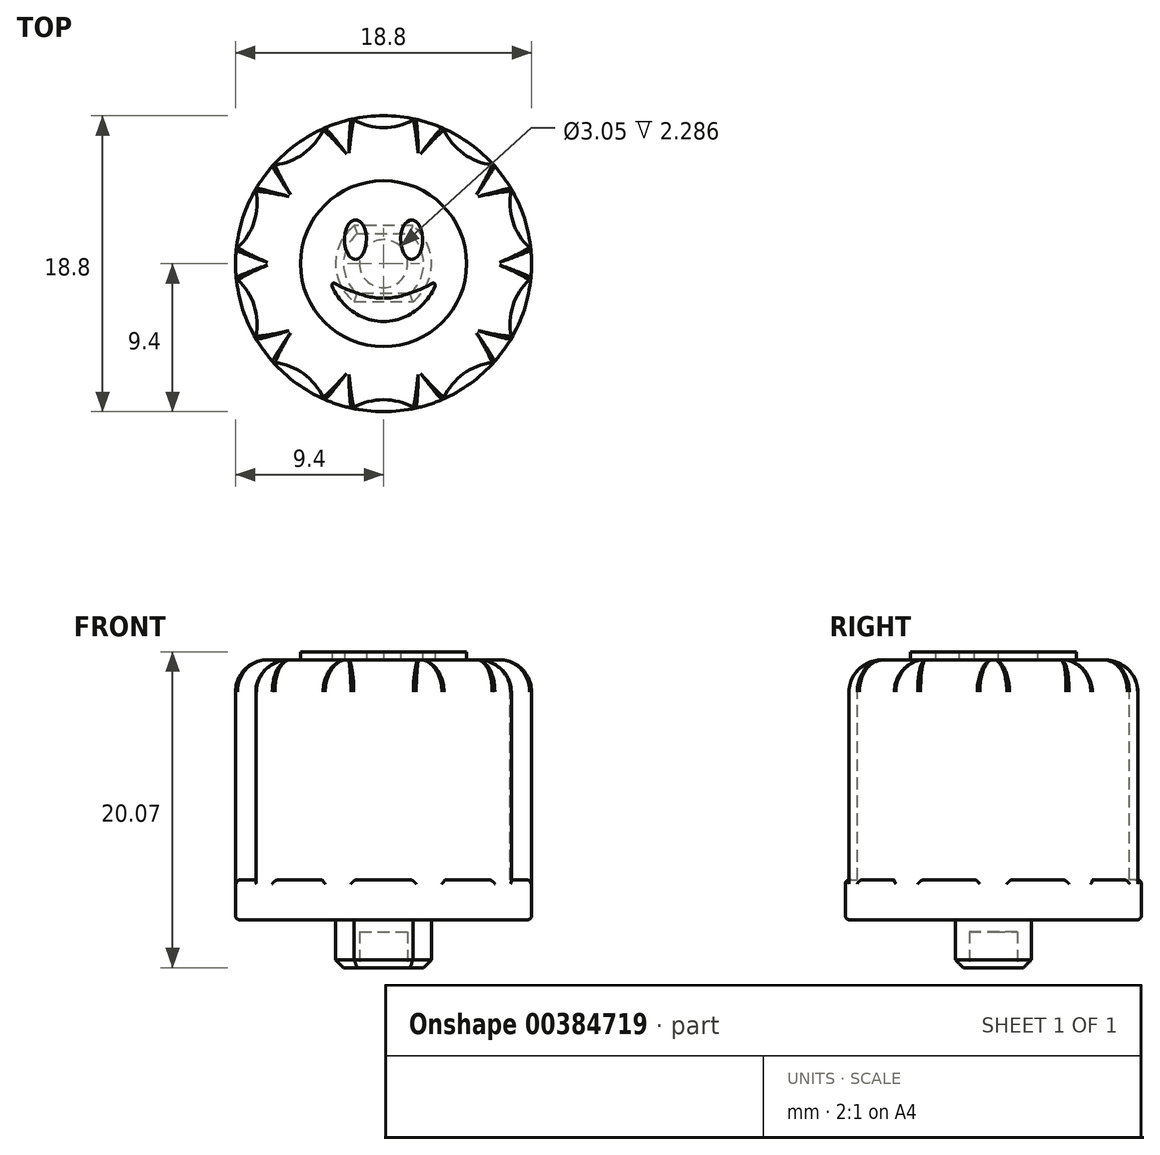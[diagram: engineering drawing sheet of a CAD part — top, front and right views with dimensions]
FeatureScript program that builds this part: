
annotation { "Feature Type Name" : "Feature", "Feature Type Description" : "" }
export const myFeature = defineFeature(function(context is Context, id is Id, definition is map)
    precondition{}
    {
        {
            var Q0;
            Q0=qCreatedBy(makeId("Top.planeOp"),FACE);
            var sketch = newSketch(context, id + "F0", { "sketchPlane" : qUnion([Q0])});
            skCircle(sketch, "E0", {"center": v(0, 0) * mm, "radius": 9.4 * mm});
            skSolve(sketch);
        }
        {
            var Q0;
            Q0=qSketchRegion(id+"F0",true);
            extrude(context, id + "F1", {"entities" : qUnion([Q0]), "depth" : 16.5 * mm});
        }
        {
            var Q0;
            Q0=makeQuery(id+"F1.opExtrude","CAP_FACE",FACE,{"disambiguationData":[OSD([sQuery(id+"F0.wireOp",EDGE,"E0")])],"isStart":false});
            var sketch = newSketch(context, id + "F2", { "sketchPlane" : qUnion([Q0])});
            skCircle(sketch, "E1.1.0", {"center": v(-7.32, 10.07) * mm, "radius": 3.81 * mm});
            skCircle(sketch, "E1.2.0", {"center": v(-11.84, 3.85) * mm, "radius": 3.81 * mm});
            skCircle(sketch, "E1.3.0", {"center": v(-11.84, -3.85) * mm, "radius": 3.81 * mm});
            skCircle(sketch, "E1.4.0", {"center": v(-7.32, -10.07) * mm, "radius": 3.81 * mm});
            skCircle(sketch, "E1.5.0", {"center": v(0, -12.45) * mm, "radius": 3.81 * mm});
            skCircle(sketch, "E1.6.0", {"center": v(7.32, -10.07) * mm, "radius": 3.81 * mm});
            skCircle(sketch, "E1.7.0", {"center": v(11.84, -3.85) * mm, "radius": 3.81 * mm});
            skCircle(sketch, "E1.8.0", {"center": v(11.84, 3.85) * mm, "radius": 3.81 * mm});
            skCircle(sketch, "E1.9.0", {"center": v(7.32, 10.07) * mm, "radius": 3.81 * mm});
            skPoint(sketch, "E1.center", {"position": v(0, 0) * mm});
            skPoint(sketch, "E2.center.orphan", {"position": v(0, 12.45) * mm});
            skCircle(sketch, "E3", {"center": v(0, 12.45) * mm, "radius": 3.81 * mm});
            skSolve(sketch);
        }
        {
            var Q0;
            Q0=qSketchRegion(id+"F2",true);
            extrude(context, id + "F3", {"entities" : qUnion([Q0]), "operationType" : NewBodyOperationType.REMOVE, "oppositeDirection" : true, "depth" : 13.97 * mm});
        }
        {
            var Q0;
            Q0=makeQuery(id+"F1.opExtrude","CAP_FACE",FACE,{"disambiguationData":[OSD([sQuery(id+"F0.wireOp",EDGE,"E0")])],"isStart":false});
            fillet(context, id + "F4", {"entities" : qUnion([Q0]), "radius" : 2.03 * mm, "tangentPropagation" : true, "allowEdgeOverflow" : false});
        }
        {
            var Q0;
            Q0=makeQuery(id+"F1.opExtrude","CAP_FACE",FACE,{"disambiguationData":[OSD([sQuery(id+"F0.wireOp",EDGE,"E0")])],"isStart":true});
            var sketch = newSketch(context, id + "F5", { "sketchPlane" : qUnion([Q0])});
            skCircle(sketch, "E4", {"center": v(0, 0) * mm, "radius": 5.33 * mm});
            skSolve(sketch);
        }
        {
            var Q0;
            Q0=qSketchRegion(id+"F5",true);
            extrude(context, id + "F6", {"entities" : qUnion([Q0]), "operationType" : NewBodyOperationType.ADD, "depth" : 8.25 * mm, "offsetDistance" : 25.4 * mm});
        }
        {
            var Q0;
            Q0=makeQuery(id+"F6.opExtrude","CAP_FACE",FACE,{"disambiguationData":[OSD([sQuery(id+"F5.wireOp",EDGE,"E4")])],"isStart":false});
            var sketch = newSketch(context, id + "F7", { "sketchPlane" : qUnion([Q0])});
            skCircle(sketch, "E5", {"center": v(0, 10.16) * mm, "radius": 5.72 * mm});
            skCircle(sketch, "E6.1.0", {"center": v(-9.66, 3.14) * mm, "radius": 5.72 * mm});
            skCircle(sketch, "E6.2.0", {"center": v(-5.97, -8.22) * mm, "radius": 5.72 * mm});
            skCircle(sketch, "E6.3.0", {"center": v(5.97, -8.22) * mm, "radius": 5.72 * mm});
            skCircle(sketch, "E6.4.0", {"center": v(9.66, 3.14) * mm, "radius": 5.72 * mm});
            skPoint(sketch, "E6.center", {"position": v(0, 0) * mm});
            skSolve(sketch);
        }
        {
            var Q0;
            Q0=qSketchRegion(id+"F7",true);
            extrude(context, id + "F8", {"entities" : qUnion([Q0]), "operationType" : NewBodyOperationType.REMOVE, "oppositeDirection" : true, "depth" : 7.62 * mm});
        }
        {
            var Q0;
            Q0=makeQuery(id+"F8.boolean.opBoolean","MERGE",FACE,{"derivedFrom":[makeQuery(id+"F1.opExtrude","CAP_FACE",FACE,{"disambiguationData":[OSD([sQuery(id+"F0.wireOp",EDGE,"E0")])],"isStart":true}),makeQuery(id+"F8.opExtrude","CAP_FACE",FACE,{"disambiguationData":[OSD([sQuery(id+"F7.wireOp",EDGE,"E5")])],"isStart":false}),makeQuery(id+"F8.opExtrude","CAP_FACE",FACE,{"disambiguationData":[OSD([sQuery(id+"F7.wireOp",EDGE,"E6.1.0")])],"isStart":false}),makeQuery(id+"F8.opExtrude","CAP_FACE",FACE,{"disambiguationData":[OSD([sQuery(id+"F7.wireOp",EDGE,"E6.2.0")])],"isStart":false}),makeQuery(id+"F8.opExtrude","CAP_FACE",FACE,{"disambiguationData":[OSD([sQuery(id+"F7.wireOp",EDGE,"E6.3.0")])],"isStart":false}),makeQuery(id+"F8.opExtrude","CAP_FACE",FACE,{"disambiguationData":[OSD([sQuery(id+"F7.wireOp",EDGE,"E6.4.0")])],"isStart":false})]});
            var sketch = newSketch(context, id + "F9", { "sketchPlane" : qUnion([Q0])});
            skCircle(sketch, "E7", {"center": v(0, 0) * mm, "radius": 6.22 * mm});
            skCircle(sketch, "E8", {"center": v(0, 0) * mm, "radius": 4.32 * mm});
            skSolve(sketch);
        }
        {
            var Q0;
            Q0=qSketchRegion(id+"F9",true);
            extrude(context, id + "F10", {"entities" : qUnion([Q0]), "operationType" : NewBodyOperationType.REMOVE, "depth" : 4.06 * mm, "offsetDistance" : 25.4 * mm});
        }
        {
            var Q0;
            Q0=makeQuery(id+"F10.boolean.opBoolean","MERGE",FACE,{"derivedFrom":[makeQuery(id+"F1.opExtrude","CAP_FACE",FACE,{"disambiguationData":[OSD([sQuery(id+"F0.wireOp",EDGE,"E0")])],"isStart":true}),makeQuery(id+"F10.opExtrude","CAP_FACE",FACE,{"disambiguationData":[OSD([sQuery(id+"F9.wireOp",EDGE,"E7"),sQuery(id+"F9.wireOp",EDGE,"E8")])],"isStart":true})]});
            var sketch = newSketch(context, id + "F11", { "sketchPlane" : qUnion([Q0])});
            skCircle(sketch, "E9", {"center": v(0, 0) * mm, "radius": 6.35 * mm});
            skSolve(sketch);
        }
        {
            var Q0;
            Q0=qSketchRegion(id+"F11",true);
            extrude(context, id + "F12", {"entities" : qUnion([Q0]), "operationType" : NewBodyOperationType.ADD, "depth" : 2.54 * mm, "offsetDistance" : 25.4 * mm});
        }
        {
            var Q0;
            Q0=makeQuery(id+"F6.opExtrude","CAP_FACE",FACE,{"disambiguationData":[OSD([sQuery(id+"F5.wireOp",EDGE,"E4")])],"isStart":false});
            fillet(context, id + "F13", {"entities" : qUnion([Q0]), "radius" : 0.5 * mm, "tangentPropagation" : true, "allowEdgeOverflow" : false});
        }
        {
            var Q0;
            Q0=makeQuery(id+"F12.opExtrude","CAP_EDGE",EDGE,{"disambiguationData":[OSD([sQuery(id+"F11.wireOp",EDGE,"E9")])],"isStart":false});
            var Q1;
            Q1=makeQuery(id+"F1.opExtrude","CAP_EDGE",EDGE,{"disambiguationData":[OSD([sQuery(id+"F0.wireOp",EDGE,"E0")])],"isStart":true});
            var Q2;
            Q2=makeQuery(id+"F3.boolean.opBoolean","INTERSECT",EDGE,{"derivedFrom":[makeQuery(id+"F1.opExtrude","SWEPT_FACE",FACE,{"disambiguationData":[OSD([sQuery(id+"F0.wireOp",EDGE,"E0")])]}),makeQuery(id+"F3.opExtrude","CAP_FACE",FACE,{"disambiguationData":[OSD([sQuery(id+"F2.wireOp",EDGE,"E1.4.0")])],"isStart":false})]});
            var Q3;
            Q3=makeQuery(id+"F3.boolean.opBoolean","INTERSECT",EDGE,{"derivedFrom":[makeQuery(id+"F1.opExtrude","SWEPT_FACE",FACE,{"disambiguationData":[OSD([sQuery(id+"F0.wireOp",EDGE,"E0")])]}),makeQuery(id+"F3.opExtrude","CAP_FACE",FACE,{"disambiguationData":[OSD([sQuery(id+"F2.wireOp",EDGE,"E1.5.0")])],"isStart":false})]});
            var Q4;
            Q4=makeQuery(id+"F3.boolean.opBoolean","INTERSECT",EDGE,{"disambiguationData":[OD(0.0)],"derivedFrom":[makeQuery(id+"F1.opExtrude","SWEPT_FACE",FACE,{"disambiguationData":[OSD([sQuery(id+"F0.wireOp",EDGE,"E0")])]}),makeQuery(id+"F3.opExtrude","SWEPT_FACE",FACE,{"disambiguationData":[OSD([sQuery(id+"F2.wireOp",EDGE,"E1.4.0")])]})]});
            var Q5;
            Q5=makeQuery(id+"F3.boolean.opBoolean","INTERSECT",EDGE,{"disambiguationData":[OD(1.0)],"derivedFrom":[makeQuery(id+"F1.opExtrude","SWEPT_FACE",FACE,{"disambiguationData":[OSD([sQuery(id+"F0.wireOp",EDGE,"E0")])]}),makeQuery(id+"F3.opExtrude","SWEPT_FACE",FACE,{"disambiguationData":[OSD([sQuery(id+"F2.wireOp",EDGE,"E1.4.0")])]})]});
            var Q6;
            Q6=makeQuery(id+"F3.boolean.opBoolean","INTERSECT",EDGE,{"disambiguationData":[OD(0.0)],"derivedFrom":[makeQuery(id+"F1.opExtrude","SWEPT_FACE",FACE,{"disambiguationData":[OSD([sQuery(id+"F0.wireOp",EDGE,"E0")])]}),makeQuery(id+"F3.opExtrude","SWEPT_FACE",FACE,{"disambiguationData":[OSD([sQuery(id+"F2.wireOp",EDGE,"E1.5.0")])]})]});
            var Q7;
            Q7=makeQuery(id+"F3.boolean.opBoolean","INTERSECT",EDGE,{"disambiguationData":[OD(1.0)],"derivedFrom":[makeQuery(id+"F1.opExtrude","SWEPT_FACE",FACE,{"disambiguationData":[OSD([sQuery(id+"F0.wireOp",EDGE,"E0")])]}),makeQuery(id+"F3.opExtrude","SWEPT_FACE",FACE,{"disambiguationData":[OSD([sQuery(id+"F2.wireOp",EDGE,"E1.5.0")])]})]});
            var Q8;
            Q8=makeQuery(id+"F3.boolean.opBoolean","INTERSECT",EDGE,{"disambiguationData":[OD(0.0)],"derivedFrom":[makeQuery(id+"F1.opExtrude","SWEPT_FACE",FACE,{"disambiguationData":[OSD([sQuery(id+"F0.wireOp",EDGE,"E0")])]}),makeQuery(id+"F3.opExtrude","SWEPT_FACE",FACE,{"disambiguationData":[OSD([sQuery(id+"F2.wireOp",EDGE,"E1.6.0")])]})]});
            var Q9;
            Q9=makeQuery(id+"F3.boolean.opBoolean","INTERSECT",EDGE,{"derivedFrom":[makeQuery(id+"F1.opExtrude","SWEPT_FACE",FACE,{"disambiguationData":[OSD([sQuery(id+"F0.wireOp",EDGE,"E0")])]}),makeQuery(id+"F3.opExtrude","CAP_FACE",FACE,{"disambiguationData":[OSD([sQuery(id+"F2.wireOp",EDGE,"E1.6.0")])],"isStart":false})]});
            var Q10;
            Q10=makeQuery(id+"F3.boolean.opBoolean","INTERSECT",EDGE,{"disambiguationData":[OD(1.0)],"derivedFrom":[makeQuery(id+"F1.opExtrude","SWEPT_FACE",FACE,{"disambiguationData":[OSD([sQuery(id+"F0.wireOp",EDGE,"E0")])]}),makeQuery(id+"F3.opExtrude","SWEPT_FACE",FACE,{"disambiguationData":[OSD([sQuery(id+"F2.wireOp",EDGE,"E1.6.0")])]})]});
            var Q11;
            Q11=makeQuery(id+"F3.boolean.opBoolean","INTERSECT",EDGE,{"disambiguationData":[OD(0.0)],"derivedFrom":[makeQuery(id+"F1.opExtrude","SWEPT_FACE",FACE,{"disambiguationData":[OSD([sQuery(id+"F0.wireOp",EDGE,"E0")])]}),makeQuery(id+"F3.opExtrude","SWEPT_FACE",FACE,{"disambiguationData":[OSD([sQuery(id+"F2.wireOp",EDGE,"E1.7.0")])]})]});
            var Q12;
            Q12=makeQuery(id+"F3.boolean.opBoolean","INTERSECT",EDGE,{"derivedFrom":[makeQuery(id+"F1.opExtrude","SWEPT_FACE",FACE,{"disambiguationData":[OSD([sQuery(id+"F0.wireOp",EDGE,"E0")])]}),makeQuery(id+"F3.opExtrude","CAP_FACE",FACE,{"disambiguationData":[OSD([sQuery(id+"F2.wireOp",EDGE,"E1.7.0")])],"isStart":false})]});
            var Q13;
            Q13=makeQuery(id+"F3.boolean.opBoolean","INTERSECT",EDGE,{"disambiguationData":[OD(1.0)],"derivedFrom":[makeQuery(id+"F1.opExtrude","SWEPT_FACE",FACE,{"disambiguationData":[OSD([sQuery(id+"F0.wireOp",EDGE,"E0")])]}),makeQuery(id+"F3.opExtrude","SWEPT_FACE",FACE,{"disambiguationData":[OSD([sQuery(id+"F2.wireOp",EDGE,"E1.7.0")])]})]});
            var Q14;
            Q14=makeQuery(id+"F3.boolean.opBoolean","INTERSECT",EDGE,{"derivedFrom":[makeQuery(id+"F1.opExtrude","SWEPT_FACE",FACE,{"disambiguationData":[OSD([sQuery(id+"F0.wireOp",EDGE,"E0")])]}),makeQuery(id+"F3.opExtrude","CAP_FACE",FACE,{"disambiguationData":[OSD([sQuery(id+"F2.wireOp",EDGE,"E1.8.0")])],"isStart":false})]});
            var Q15;
            Q15=makeQuery(id+"F3.boolean.opBoolean","INTERSECT",EDGE,{"disambiguationData":[OD(0.0)],"derivedFrom":[makeQuery(id+"F1.opExtrude","SWEPT_FACE",FACE,{"disambiguationData":[OSD([sQuery(id+"F0.wireOp",EDGE,"E0")])]}),makeQuery(id+"F3.opExtrude","SWEPT_FACE",FACE,{"disambiguationData":[OSD([sQuery(id+"F2.wireOp",EDGE,"E1.8.0")])]})]});
            var Q16;
            Q16=makeQuery(id+"F3.boolean.opBoolean","INTERSECT",EDGE,{"disambiguationData":[OD(1.0)],"derivedFrom":[makeQuery(id+"F1.opExtrude","SWEPT_FACE",FACE,{"disambiguationData":[OSD([sQuery(id+"F0.wireOp",EDGE,"E0")])]}),makeQuery(id+"F3.opExtrude","SWEPT_FACE",FACE,{"disambiguationData":[OSD([sQuery(id+"F2.wireOp",EDGE,"E1.8.0")])]})]});
            var Q17;
            Q17=makeQuery(id+"F3.boolean.opBoolean","INTERSECT",EDGE,{"disambiguationData":[OD(1.0)],"derivedFrom":[makeQuery(id+"F1.opExtrude","SWEPT_FACE",FACE,{"disambiguationData":[OSD([sQuery(id+"F0.wireOp",EDGE,"E0")])]}),makeQuery(id+"F3.opExtrude","SWEPT_FACE",FACE,{"disambiguationData":[OSD([sQuery(id+"F2.wireOp",EDGE,"E1.9.0")])]})]});
            var Q18;
            Q18=makeQuery(id+"F3.boolean.opBoolean","INTERSECT",EDGE,{"derivedFrom":[makeQuery(id+"F1.opExtrude","SWEPT_FACE",FACE,{"disambiguationData":[OSD([sQuery(id+"F0.wireOp",EDGE,"E0")])]}),makeQuery(id+"F3.opExtrude","CAP_FACE",FACE,{"disambiguationData":[OSD([sQuery(id+"F2.wireOp",EDGE,"E1.9.0")])],"isStart":false})]});
            var Q19;
            Q19=makeQuery(id+"F3.boolean.opBoolean","INTERSECT",EDGE,{"disambiguationData":[OD(0.0)],"derivedFrom":[makeQuery(id+"F1.opExtrude","SWEPT_FACE",FACE,{"disambiguationData":[OSD([sQuery(id+"F0.wireOp",EDGE,"E0")])]}),makeQuery(id+"F3.opExtrude","SWEPT_FACE",FACE,{"disambiguationData":[OSD([sQuery(id+"F2.wireOp",EDGE,"E1.9.0")])]})]});
            var Q20;
            Q20=makeQuery(id+"F3.boolean.opBoolean","INTERSECT",EDGE,{"disambiguationData":[OD(1.0)],"derivedFrom":[makeQuery(id+"F1.opExtrude","SWEPT_FACE",FACE,{"disambiguationData":[OSD([sQuery(id+"F0.wireOp",EDGE,"E0")])]}),makeQuery(id+"F3.opExtrude","SWEPT_FACE",FACE,{"disambiguationData":[OSD([sQuery(id+"F2.wireOp",EDGE,"E3")])]})]});
            var Q21;
            Q21=makeQuery(id+"F3.boolean.opBoolean","INTERSECT",EDGE,{"derivedFrom":[makeQuery(id+"F1.opExtrude","SWEPT_FACE",FACE,{"disambiguationData":[OSD([sQuery(id+"F0.wireOp",EDGE,"E0")])]}),makeQuery(id+"F3.opExtrude","CAP_FACE",FACE,{"disambiguationData":[OSD([sQuery(id+"F2.wireOp",EDGE,"E3")])],"isStart":false})]});
            var Q22;
            Q22=makeQuery(id+"F3.boolean.opBoolean","INTERSECT",EDGE,{"disambiguationData":[OD(0.0)],"derivedFrom":[makeQuery(id+"F1.opExtrude","SWEPT_FACE",FACE,{"disambiguationData":[OSD([sQuery(id+"F0.wireOp",EDGE,"E0")])]}),makeQuery(id+"F3.opExtrude","SWEPT_FACE",FACE,{"disambiguationData":[OSD([sQuery(id+"F2.wireOp",EDGE,"E3")])]})]});
            var Q23;
            Q23=makeQuery(id+"F3.boolean.opBoolean","INTERSECT",EDGE,{"derivedFrom":[makeQuery(id+"F1.opExtrude","SWEPT_FACE",FACE,{"disambiguationData":[OSD([sQuery(id+"F0.wireOp",EDGE,"E0")])]}),makeQuery(id+"F3.opExtrude","CAP_FACE",FACE,{"disambiguationData":[OSD([sQuery(id+"F2.wireOp",EDGE,"E1.1.0")])],"isStart":false})]});
            var Q24;
            Q24=makeQuery(id+"F3.boolean.opBoolean","INTERSECT",EDGE,{"disambiguationData":[OD(1.0)],"derivedFrom":[makeQuery(id+"F1.opExtrude","SWEPT_FACE",FACE,{"disambiguationData":[OSD([sQuery(id+"F0.wireOp",EDGE,"E0")])]}),makeQuery(id+"F3.opExtrude","SWEPT_FACE",FACE,{"disambiguationData":[OSD([sQuery(id+"F2.wireOp",EDGE,"E1.1.0")])]})]});
            var Q25;
            Q25=makeQuery(id+"F3.boolean.opBoolean","INTERSECT",EDGE,{"disambiguationData":[OD(0.0)],"derivedFrom":[makeQuery(id+"F1.opExtrude","SWEPT_FACE",FACE,{"disambiguationData":[OSD([sQuery(id+"F0.wireOp",EDGE,"E0")])]}),makeQuery(id+"F3.opExtrude","SWEPT_FACE",FACE,{"disambiguationData":[OSD([sQuery(id+"F2.wireOp",EDGE,"E1.1.0")])]})]});
            var Q26;
            Q26=makeQuery(id+"F3.boolean.opBoolean","INTERSECT",EDGE,{"disambiguationData":[OD(1.0)],"derivedFrom":[makeQuery(id+"F1.opExtrude","SWEPT_FACE",FACE,{"disambiguationData":[OSD([sQuery(id+"F0.wireOp",EDGE,"E0")])]}),makeQuery(id+"F3.opExtrude","SWEPT_FACE",FACE,{"disambiguationData":[OSD([sQuery(id+"F2.wireOp",EDGE,"E1.2.0")])]})]});
            var Q27;
            Q27=makeQuery(id+"F3.boolean.opBoolean","INTERSECT",EDGE,{"derivedFrom":[makeQuery(id+"F1.opExtrude","SWEPT_FACE",FACE,{"disambiguationData":[OSD([sQuery(id+"F0.wireOp",EDGE,"E0")])]}),makeQuery(id+"F3.opExtrude","CAP_FACE",FACE,{"disambiguationData":[OSD([sQuery(id+"F2.wireOp",EDGE,"E1.2.0")])],"isStart":false})]});
            var Q28;
            Q28=makeQuery(id+"F3.boolean.opBoolean","INTERSECT",EDGE,{"disambiguationData":[OD(0.0)],"derivedFrom":[makeQuery(id+"F1.opExtrude","SWEPT_FACE",FACE,{"disambiguationData":[OSD([sQuery(id+"F0.wireOp",EDGE,"E0")])]}),makeQuery(id+"F3.opExtrude","SWEPT_FACE",FACE,{"disambiguationData":[OSD([sQuery(id+"F2.wireOp",EDGE,"E1.2.0")])]})]});
            var Q29;
            Q29=makeQuery(id+"F3.boolean.opBoolean","INTERSECT",EDGE,{"disambiguationData":[OD(1.0)],"derivedFrom":[makeQuery(id+"F1.opExtrude","SWEPT_FACE",FACE,{"disambiguationData":[OSD([sQuery(id+"F0.wireOp",EDGE,"E0")])]}),makeQuery(id+"F3.opExtrude","SWEPT_FACE",FACE,{"disambiguationData":[OSD([sQuery(id+"F2.wireOp",EDGE,"E1.3.0")])]})]});
            var Q30;
            Q30=makeQuery(id+"F3.boolean.opBoolean","INTERSECT",EDGE,{"derivedFrom":[makeQuery(id+"F1.opExtrude","SWEPT_FACE",FACE,{"disambiguationData":[OSD([sQuery(id+"F0.wireOp",EDGE,"E0")])]}),makeQuery(id+"F3.opExtrude","CAP_FACE",FACE,{"disambiguationData":[OSD([sQuery(id+"F2.wireOp",EDGE,"E1.3.0")])],"isStart":false})]});
            var Q31;
            Q31=makeQuery(id+"F3.boolean.opBoolean","INTERSECT",EDGE,{"disambiguationData":[OD(0.0)],"derivedFrom":[makeQuery(id+"F1.opExtrude","SWEPT_FACE",FACE,{"disambiguationData":[OSD([sQuery(id+"F0.wireOp",EDGE,"E0")])]}),makeQuery(id+"F3.opExtrude","SWEPT_FACE",FACE,{"disambiguationData":[OSD([sQuery(id+"F2.wireOp",EDGE,"E1.3.0")])]})]});
            fillet(context, id + "F14", {"entities" : qUnion([Q0, Q1, Q2, Q3, Q4, Q5, Q6, Q7, Q8, Q9, Q10, Q11, Q12, Q13, Q14, Q15, Q16, Q17, Q18, Q19, Q20, Q21, Q22, Q23, Q24, Q25, Q26, Q27, Q28, Q29, Q30, Q31]), "radius" : 0.25 * mm, "tangentPropagation" : true, "allowEdgeOverflow" : false});
        }
        {
            var Q0;
            Q0=makeQuery(id+"F6.opExtrude","CAP_FACE",FACE,{"disambiguationData":[OSD([sQuery(id+"F5.wireOp",EDGE,"E4")])],"isStart":false});
            var sketch = newSketch(context, id + "F15", { "sketchPlane" : qUnion([Q0])});
            skCircle(sketch, "E10", {"center": v(0, 0) * mm, "radius": 1.52 * mm});
            skSolve(sketch);
        }
        {
            var Q0;
            Q0=qSketchRegion(id+"F15",true);
            extrude(context, id + "F16", {"entities" : qUnion([Q0]), "operationType" : NewBodyOperationType.REMOVE, "oppositeDirection" : true, "depth" : 7.37 * mm, "offsetDistance" : 25.4 * mm});
        }
        {
            var Q0;
            Q0=makeQuery(id+"F6.opExtrude","CAP_FACE",FACE,{"disambiguationData":[OSD([sQuery(id+"F5.wireOp",EDGE,"E4")])],"isStart":false});
            var sketch = newSketch(context, id + "F17", { "sketchPlane" : qUnion([Q0])});
            skArc(sketch, "E11", {"start": v(0.87, -2.92) * mm, "mid": v(0, 3.05) * mm, "end": v(-0.87, -2.92) * mm});
            skArc(sketch, "E12", {"start": v(-0.87, -2.92) * mm, "mid": v(0, -3.5) * mm, "end": v(0.87, -2.92) * mm});
            skCircle(sketch, "E13", {"center": v(0, 0) * mm, "radius": 1.52 * mm});
            skArc(sketch, "E14.1.0", {"start": v(0.87, 2.92) * mm, "mid": v(0, 3.5) * mm, "end": v(-0.87, 2.92) * mm});
            skSolve(sketch);
        }
        {
            var Q0;
            Q0=qSketchRegion(id+"F17",true);
            extrude(context, id + "F18", {"entities" : qUnion([Q0]), "operationType" : NewBodyOperationType.ADD, "depth" : 3.05 * mm, "offsetDistance" : 25.4 * mm});
        }
        {
            var Q0;
            Q0=makeQuery(id+"F18.opExtrude","CAP_FACE",FACE,{"disambiguationData":[OSD([sQuery(id+"F17.wireOp",EDGE,"E11"),sQuery(id+"F17.wireOp",EDGE,"E12"),sQuery(id+"F17.wireOp",EDGE,"E13")])],"isStart":false});
            fillet(context, id + "F19", {"entities" : qUnion([Q0]), "radius" : 0.5 * mm, "tangentPropagation" : true, "allowEdgeOverflow" : false});
        }
        {
            var Q0;
            Q0=makeQuery(id+"F10.boolean.opBoolean","MERGE",FACE,{"derivedFrom":[makeQuery(id+"F1.opExtrude","CAP_FACE",FACE,{"disambiguationData":[OSD([sQuery(id+"F0.wireOp",EDGE,"E0")])],"isStart":true}),makeQuery(id+"F10.opExtrude","CAP_FACE",FACE,{"disambiguationData":[OSD([sQuery(id+"F9.wireOp",EDGE,"E7"),sQuery(id+"F9.wireOp",EDGE,"E8")])],"isStart":true})]});
            var sketch = newSketch(context, id + "F20", { "sketchPlane" : qUnion([Q0])});
            skLineSegment(sketch, "E15.bottom", {"start": v(-12.19, 12.59) * mm, "end": v(12.3, 12.59) * mm});
            skLineSegment(sketch, "E15.top", {"start": v(-12.19, -14.05) * mm, "end": v(12.3, -14.05) * mm});
            skLineSegment(sketch, "E15.left", {"start": v(-12.19, 12.59) * mm, "end": v(-12.19, -14.05) * mm});
            skLineSegment(sketch, "E15.right", {"start": v(12.3, 12.59) * mm, "end": v(12.3, -14.05) * mm});
            skSolve(sketch);
        }
        {
            var Q0;
            Q0=qSketchRegion(id+"F20",true);
            extrude(context, id + "F21", {"entities" : qUnion([Q0]), "operationType" : NewBodyOperationType.REMOVE, "depth" : 25.4 * mm, "offsetDistance" : 25.4 * mm});
        }
        {
            var Q0;
            Q0=makeQuery(id+"F21.boolean.opBoolean","MERGE",FACE,{"derivedFrom":[makeQuery(id+"F10.boolean.opBoolean","MERGE",FACE,{"derivedFrom":[makeQuery(id+"F1.opExtrude","CAP_FACE",FACE,{"disambiguationData":[OSD([sQuery(id+"F0.wireOp",EDGE,"E0")])],"isStart":true}),makeQuery(id+"F10.opExtrude","CAP_FACE",FACE,{"disambiguationData":[OSD([sQuery(id+"F9.wireOp",EDGE,"E7"),sQuery(id+"F9.wireOp",EDGE,"E8")])],"isStart":true})]}),makeQuery(id+"F21.opExtrude","CAP_FACE",FACE,{"disambiguationData":[OSD([sQuery(id+"F20.wireOp",EDGE,"E15.bottom"),sQuery(id+"F20.wireOp",EDGE,"E15.top"),sQuery(id+"F20.wireOp",EDGE,"E15.left"),sQuery(id+"F20.wireOp",EDGE,"E15.right")])],"isStart":true})]});
            var sketch = newSketch(context, id + "F22", { "sketchPlane" : qUnion([Q0])});
            skArc(sketch, "E16", {"start": v(-1.86, 2.41) * mm, "mid": v(-3.05, 0) * mm, "end": v(-1.86, -2.41) * mm});
            skLineSegment(sketch, "E17", {"start": v(-1.86, 2.41) * mm, "end": v(1.86, 2.41) * mm});
            skLineSegment(sketch, "E18", {"start": v(1.86, -2.41) * mm, "end": v(-1.86, -2.41) * mm});
            skArc(sketch, "E19.trimOffspring", {"start": v(1.86, -2.41) * mm, "mid": v(3.05, 0) * mm, "end": v(1.86, 2.41) * mm});
            skSolve(sketch);
        }
        {
            var Q0;
            Q0=qSketchRegion(id+"F22",true);
            extrude(context, id + "F23", {"entities" : qUnion([Q0]), "operationType" : NewBodyOperationType.ADD, "depth" : 3.05 * mm, "offsetDistance" : 25.4 * mm});
        }
        {
            var Q0;
            Q0=makeQuery(id+"F23.opExtrude","CAP_FACE",FACE,{"disambiguationData":[OSD([sQuery(id+"F22.wireOp",EDGE,"E16"),sQuery(id+"F22.wireOp",EDGE,"E17"),sQuery(id+"F22.wireOp",EDGE,"E18"),sQuery(id+"F22.wireOp",EDGE,"E19.trimOffspring")])],"isStart":false});
            var sketch = newSketch(context, id + "F24", { "sketchPlane" : qUnion([Q0])});
            skCircle(sketch, "E20", {"center": v(0, 0) * mm, "radius": 1.52 * mm});
            skSolve(sketch);
        }
        {
            var Q0;
            Q0=qSketchRegion(id+"F24",true);
            extrude(context, id + "F25", {"entities" : qUnion([Q0]), "operationType" : NewBodyOperationType.REMOVE, "oppositeDirection" : true, "depth" : 2.3 * mm, "offsetDistance" : 25.4 * mm});
        }
        {
            var Q0;
            Q0=makeQuery(id+"F1.opExtrude","CAP_FACE",FACE,{"disambiguationData":[OSD([sQuery(id+"F0.wireOp",EDGE,"E0")])],"isStart":false});
            var sketch = newSketch(context, id + "F26", { "sketchPlane" : qUnion([Q0])});
            skCircle(sketch, "E21", {"center": v(0, 0) * mm, "radius": 5.27 * mm});
            skEllipse(sketch, "E22", {"center": v(-1.79, 1.54) * mm, "majorRadius": 1.26 * mm, "minorRadius": 0.7 * mm, "majorAxis": v(0, -1)});
            skFitSpline(sketch, "E23", {"points": [v(0, -2.19) * mm, v(-1.79, -1.83) * mm, v(-3.42, -0.99) * mm], "startDerivative": vector(-4.01, -0.12) * mm, "endDerivative": vector(-2.65, 2.5) * mm});
            skFitSpline(sketch, "E24", {"points": [v(-3.42, -0.99) * mm, v(-2.03, -2.98) * mm, v(0, -3.67) * mm], "startDerivative": vector(1.34, -4.72) * mm, "endDerivative": vector(5.1, -0.21) * mm});
            skEllipse(sketch, "E25.MirrorC", {"center": v(1.79, 1.54) * mm, "majorRadius": 1.26 * mm, "minorRadius": 0.7 * mm, "majorAxis": v(0, -1)});
            skFitSpline(sketch, "E26.MirrorCS", {"points": [v(0, -2.19) * mm, v(1.79, -1.83) * mm, v(3.42, -0.99) * mm], "startDerivative": vector(4.01, -0.12) * mm, "endDerivative": vector(2.65, 2.5) * mm});
            skFitSpline(sketch, "E27.MirrorCS", {"points": [v(3.42, -0.99) * mm, v(2.03, -2.98) * mm, v(0, -3.67) * mm], "startDerivative": vector(-1.34, -4.72) * mm, "endDerivative": vector(-5.1, -0.21) * mm});
            skSolve(sketch);
        }
        {
            var Q0;
            Q0=qSketchRegion(id+"F26",true);
            extrude(context, id + "F27", {"entities" : qUnion([Q0]), "operationType" : NewBodyOperationType.ADD, "depth" : 0.5 * mm, "offsetDistance" : 25.4 * mm});
        }
        {
            var Q0;
            Q0=makeQuery(id+"F23.opExtrude","CAP_EDGE",EDGE,{"disambiguationData":[OSD([sQuery(id+"F22.wireOp",EDGE,"E18")])],"isStart":false});
            var Q1;
            Q1=makeQuery(id+"F23.opExtrude","CAP_EDGE",EDGE,{"disambiguationData":[OSD([sQuery(id+"F22.wireOp",EDGE,"E19.trimOffspring")])],"isStart":false});
            var Q2;
            Q2=makeQuery(id+"F23.opExtrude","CAP_EDGE",EDGE,{"disambiguationData":[OSD([sQuery(id+"F22.wireOp",EDGE,"E16")])],"isStart":false});
            var Q3;
            Q3=makeQuery(id+"F23.opExtrude","CAP_EDGE",EDGE,{"disambiguationData":[OSD([sQuery(id+"F22.wireOp",EDGE,"E17")])],"isStart":false});
            chamfer(context, id + "F28", {"entities" : qUnion([Q0, Q1, Q2, Q3]), "width" : 0.5 * mm, "tangentPropagation" : true});
        }
        {
            var Q0;
            Q0=makeQuery(id+"F27.opExtrude","SWEPT_EDGE",EDGE,{"disambiguationData":[OSD([sQuery(id+"F26.wireOp",EDGE,"E23"),sQuery(id+"F26.wireOp",EDGE,"E24")])]});
            var Q1;
            Q1=makeQuery(id+"F27.opExtrude","SWEPT_EDGE",EDGE,{"disambiguationData":[OSD([sQuery(id+"F26.wireOp",EDGE,"E26.MirrorCS"),sQuery(id+"F26.wireOp",EDGE,"E27.MirrorCS")])]});
            fillet(context, id + "F29", {"entities" : qUnion([Q0, Q1]), "radius" : 0.13 * mm, "tangentPropagation" : true, "allowEdgeOverflow" : false});
        }
    });
